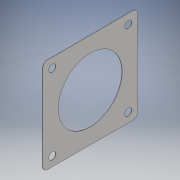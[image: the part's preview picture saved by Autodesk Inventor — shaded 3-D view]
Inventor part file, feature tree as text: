
AUTODESK INVENTOR PART (.ipt)
format: ipt  version: 2018 (Build 220112000, 112)  size: 119,808 bytes
history: native  units: mm
features: extrude x1, sketch x1
ambient origin geometry x8: Origin, YZ Plane, XZ Plane, XY Plane, X Axis, Y Axis, Z Axis, Center Point
bodies: Solid1 (feature_tree)
feature tree (2):
  extrude  "Extrusion1"  Depth=40.0mm
  sketch  "Sketch1"  dims[d0=40.0mm d1=40.0mm d2=3.0mm d3=27.0mm d4=32.0mm d5=32.0mm d6=2.0mm d7=0.2mm d8=0.0mm]
